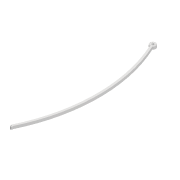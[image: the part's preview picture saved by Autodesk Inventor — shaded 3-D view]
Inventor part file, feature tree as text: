
AUTODESK INVENTOR PART (.ipt)
format: ipt  version: 2022 (Build 260153000, 153)  size: 161,792 bytes
history: native  units: mm
features: extrude x4, sketch x4, projected_geometry x3, pattern_circular x1
ambient origin geometry x8: Origin, YZ Plane, XZ Plane, XY Plane, X Axis, Y Axis, Z Axis, Center Point
bodies: Solid1 (feature_tree)
feature tree (12):
  extrude  "Extrusion1"  Depth=8.0mm
  extrude  "Extrusion5"  Depth=3.0mm
  extrude  "Extrusion6"  Depth=600.0mm
  pattern_circular  "Circular Pattern1"  Count=60  [1 undecoded]
  extrude  "Extrusion2"  Depth=8.0mm
  sketch  "Sketch1"  dims[d0=8.0mm d1=521.938mm]
  sketch  "Sketch2"  dims[d2=3.0mm d3=3.0mm]
  projected_geometry  "Projected Loop1"
  sketch  "Sketch5"  dims[d4=10.0mm d5=0.0mm d24=600.0mm d25=600.0mm]
  projected_geometry  "Projected Loop2"
  sketch  "Sketch6"  dims[d26=3.0mm d27=3.0mm d28=10.0mm d29=0.0mm d45=22.0mm d46=10.0mm d47=0.0mm d48=2.2mm d49=8.0mm d50=100.0mm d51=0.0mm d52=80.0mm d53=360.0deg d55=8.5mm]
  projected_geometry  "Projected Loop3"
note: 1 required parameter value undecoded (feature->parameter linkage not recoverable at this tier; creation-order binding heuristic only, values carry confidence <= 0.55)
